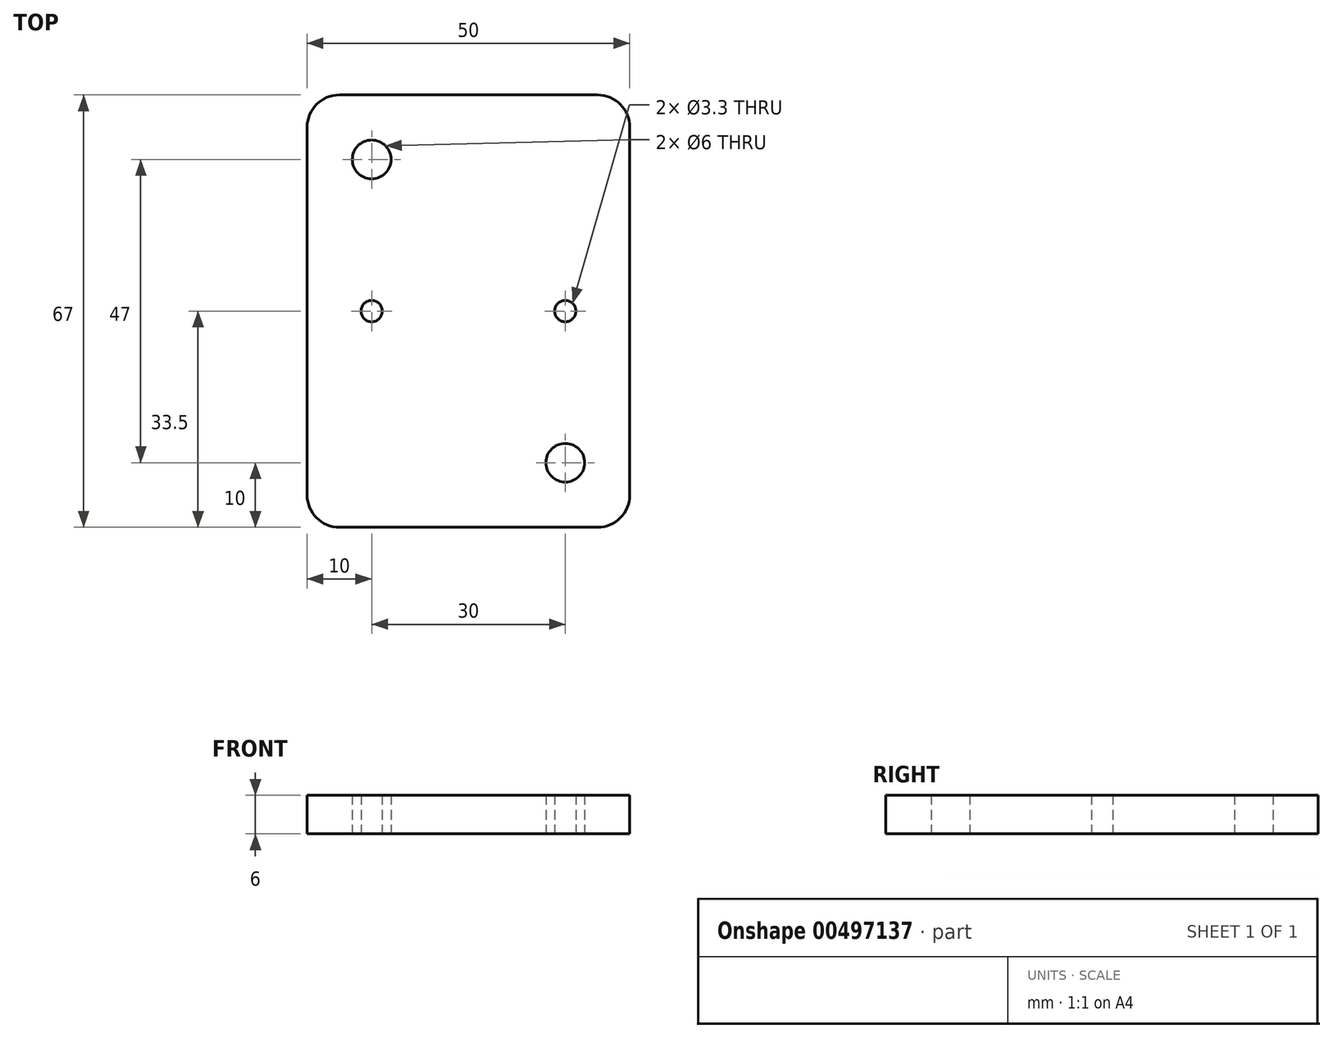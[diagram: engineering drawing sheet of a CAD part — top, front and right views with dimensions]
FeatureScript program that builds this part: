
annotation { "Feature Type Name" : "Feature", "Feature Type Description" : "" }
export const myFeature = defineFeature(function(context is Context, id is Id, definition is map)
    precondition{}
    {
        {
            var Q0;
            Q0=qCreatedBy(makeId("Top.planeOp"),FACE);
            var sketch = newSketch(context, id + "F0", { "sketchPlane" : qUnion([Q0])});
            skLineSegment(sketch, "E0.bottom", {"start": v(20, 33.5) * mm, "end": v(-20, 33.5) * mm});
            skLineSegment(sketch, "E0.top", {"start": v(20, -33.5) * mm, "end": v(-20, -33.5) * mm});
            skLineSegment(sketch, "E0.left", {"start": v(25, 28.5) * mm, "end": v(25, -28.5) * mm});
            skLineSegment(sketch, "E0.right", {"start": v(-25, 28.5) * mm, "end": v(-25, -28.5) * mm});
            skPoint(sketch, "E0.middle", {"position": v(0, 0) * mm});
            skPoint(sketch, "E1", {"position": v(15, -23.5) * mm});
            skPoint(sketch, "E2", {"position": v(-15, 23.5) * mm});
            skPoint(sketch, "E3", {"position": v(-15, 0) * mm});
            skPoint(sketch, "E4", {"position": v(15, 0) * mm});
            skPoint(sketch, "E5.visualSharp", {"position": v(-25, 33.5) * mm});
            skArc(sketch, "E5.filletArc", {"start": v(-20, 33.5) * mm, "mid": v(-23.54, 32.04) * mm, "end": v(-25, 28.5) * mm});
            skPoint(sketch, "E6.visualSharp", {"position": v(25, 33.5) * mm});
            skArc(sketch, "E6.filletArc", {"start": v(25, 28.5) * mm, "mid": v(23.54, 32.04) * mm, "end": v(20, 33.5) * mm});
            skPoint(sketch, "E7.visualSharp", {"position": v(25, -33.5) * mm});
            skArc(sketch, "E7.filletArc", {"start": v(20, -33.5) * mm, "mid": v(23.54, -32.04) * mm, "end": v(25, -28.5) * mm});
            skPoint(sketch, "E8.visualSharp", {"position": v(-25, -33.5) * mm});
            skArc(sketch, "E8.filletArc", {"start": v(-25, -28.5) * mm, "mid": v(-23.54, -32.04) * mm, "end": v(-20, -33.5) * mm});
            skSolve(sketch);
        }
        {
            var Q0;
            Q0=makeQuery(id+"F0.imprint","IMPRINT",FACE,{"disambiguationData":[TD([[makeQuery(id+"F0.imprint","IMPRINT",EDGE,{"derivedFrom":sQuery(id+"F0.wireOp",EDGE,"E0.bottom")}),1.0]])]});
            extrude(context, id + "F1", {"entities" : qUnion([Q0]), "depth" : 6 * mm, "offsetDistance" : 25 * mm});
        }
        {
            var Q0;
            Q0=sQuery(id+"F0.wireOp",VERTEX,"E3");
            var Q1;
            Q1=sQuery(id+"F0.wireOp",VERTEX,"E4");
            var Q2;
            Q2=makeQuery(id+"F1.opExtrude","SWEPT_BODY",BODY,{"disambiguationData":[OSD([sQuery(id+"F0.wireOp",EDGE,"E0.bottom"),sQuery(id+"F0.wireOp",EDGE,"E0.top"),sQuery(id+"F0.wireOp",EDGE,"E0.left"),sQuery(id+"F0.wireOp",EDGE,"E0.right"),sQuery(id+"F0.wireOp",EDGE,"E5.filletArc"),sQuery(id+"F0.wireOp",EDGE,"E6.filletArc"),sQuery(id+"F0.wireOp",EDGE,"E7.filletArc"),sQuery(id+"F0.wireOp",EDGE,"E8.filletArc")])]});
            hole(context, id + "F2", {"style" : HoleStyle.SIMPLE, "endStyle" : HoleEndStyle.THROUGH, "oppositeDirection" : true, "standardTappedOrClearance" : lookupTablePath({ "standard" : "ISO", "fit" : "Normal", "size" : "M3", "type" : "Clearance" }), "standardBlindInLast" : lookupTablePath({ "fit" : "Standard", "standard" : "ISO", "size" : "M3", "type" : "Clearance" }), "holeDiameter" : 3.3 * mm, "majorDiameter" : 5 * mm, "isTappedThrough" : true, "tappedDepth" : 6.2 * mm, "tapClearance" : 3, "locations" : qUnion([Q0, Q1]), "scope" : qUnion([Q2])});
        }
        {
            var Q0;
            Q0=sQuery(id+"F0.wireOp",VERTEX,"E2");
            var Q1;
            Q1=sQuery(id+"F0.wireOp",VERTEX,"E1");
            var Q2;
            Q2=makeQuery(id+"F1.opExtrude","SWEPT_BODY",BODY,{"disambiguationData":[OSD([sQuery(id+"F0.wireOp",EDGE,"E0.bottom"),sQuery(id+"F0.wireOp",EDGE,"E0.top"),sQuery(id+"F0.wireOp",EDGE,"E0.left"),sQuery(id+"F0.wireOp",EDGE,"E0.right"),sQuery(id+"F0.wireOp",EDGE,"E5.filletArc"),sQuery(id+"F0.wireOp",EDGE,"E6.filletArc"),sQuery(id+"F0.wireOp",EDGE,"E7.filletArc"),sQuery(id+"F0.wireOp",EDGE,"E8.filletArc")])]});
            hole(context, id + "F3", {"style" : HoleStyle.SIMPLE, "endStyle" : HoleEndStyle.THROUGH, "oppositeDirection" : true, "holeDiameter" : 6 * mm, "majorDiameter" : 5 * mm, "isTappedThrough" : true, "tappedDepth" : 6.2 * mm, "tapClearance" : 3, "locations" : qUnion([Q0, Q1]), "scope" : qUnion([Q2])});
        }
    });
